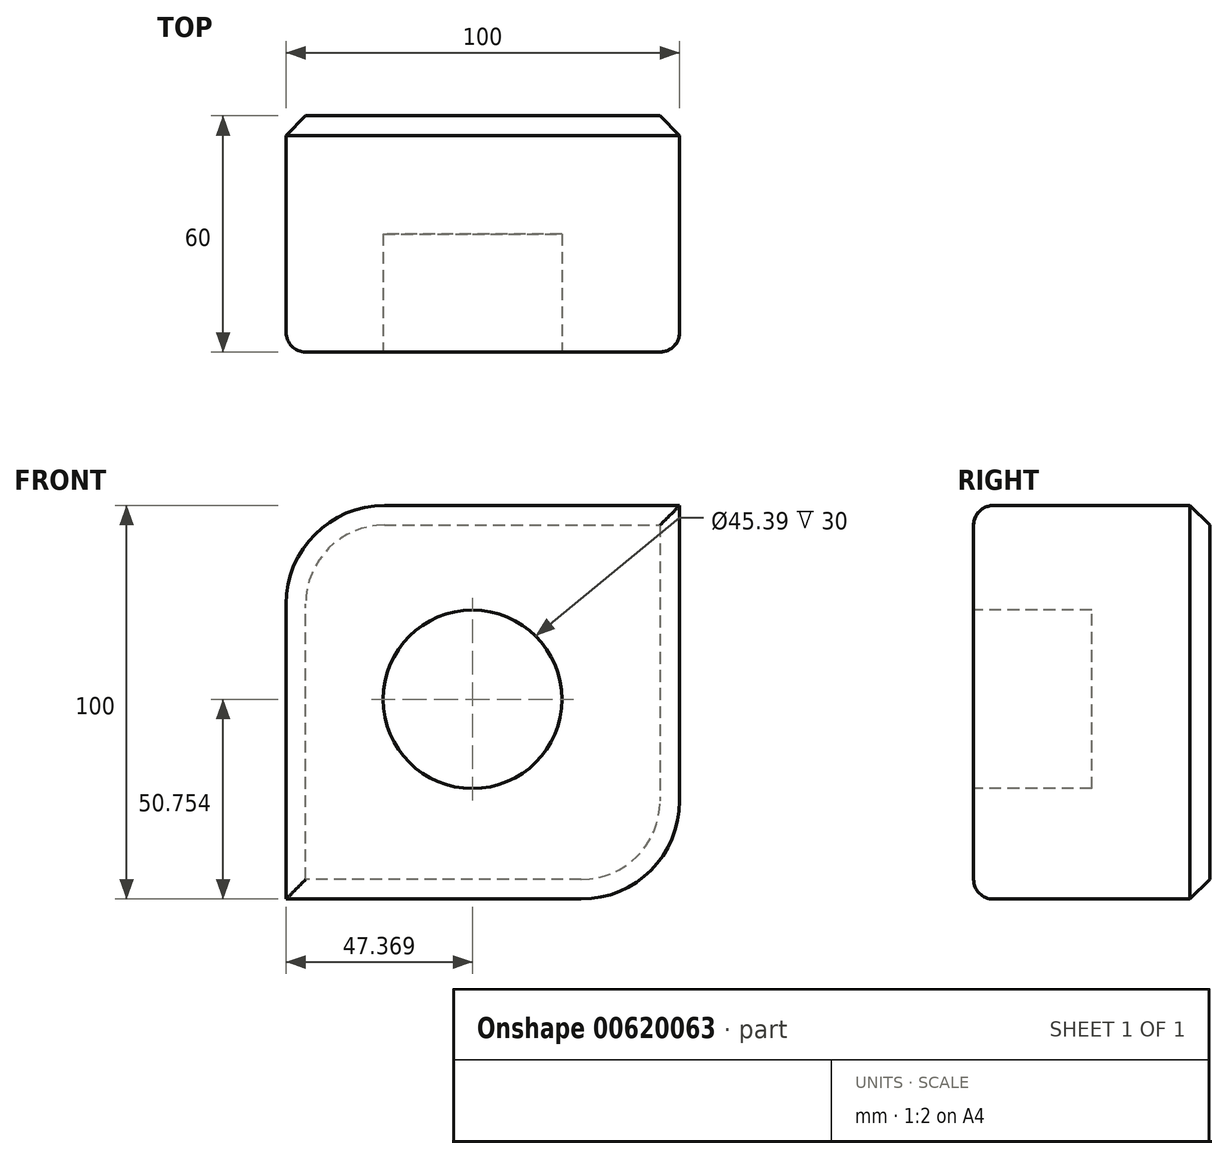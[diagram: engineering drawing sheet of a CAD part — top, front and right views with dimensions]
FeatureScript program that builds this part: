
annotation { "Feature Type Name" : "Feature", "Feature Type Description" : "" }
export const myFeature = defineFeature(function(context is Context, id is Id, definition is map)
    precondition{}
    {
        {
            var Q0;
            Q0=qCreatedBy(makeId("Front.planeOp"),FACE);
            var sketch = newSketch(context, id + "F0", { "sketchPlane" : qUnion([Q0])});
            skLineSegment(sketch, "E0.bottom", {"start": v(-16.3, 72.19) * mm, "end": v(58.7, 72.19) * mm});
            skLineSegment(sketch, "E0.top", {"start": v(-41.3, -27.81) * mm, "end": v(33.7, -27.81) * mm});
            skLineSegment(sketch, "E0.left", {"start": v(-41.3, 47.19) * mm, "end": v(-41.3, -27.81) * mm});
            skLineSegment(sketch, "E0.right", {"start": v(58.7, 72.19) * mm, "end": v(58.7, -2.81) * mm});
            skPoint(sketch, "E1.visualSharp", {"position": v(-41.3, 72.19) * mm});
            skArc(sketch, "E1.filletArc", {"start": v(-16.3, 72.19) * mm, "mid": v(-33.98, 64.87) * mm, "end": v(-41.3, 47.19) * mm});
            skPoint(sketch, "E2.visualSharp", {"position": v(58.7, -27.81) * mm});
            skArc(sketch, "E2.filletArc", {"start": v(33.7, -27.81) * mm, "mid": v(51.38, -20.5) * mm, "end": v(58.7, -2.81) * mm});
            skSolve(sketch);
        }
        {
            var Q0;
            Q0 = qSketchRegion(id + "F0", true);
            extrude(context, id + "F1", {"entities" : qUnion([Q0]), "depth" : 60 * mm, "offsetDistance" : 25 * mm});
        }
        {
            var Q0;
            Q0=makeQuery(id+"F1.opExtrude","CAP_FACE",FACE,{"disambiguationData":[OSD([sQuery(id+"F0.wireOp",EDGE,"E0.bottom"),sQuery(id+"F0.wireOp",EDGE,"E0.top"),sQuery(id+"F0.wireOp",EDGE,"E0.left"),sQuery(id+"F0.wireOp",EDGE,"E0.right"),sQuery(id+"F0.wireOp",EDGE,"E1.filletArc"),sQuery(id+"F0.wireOp",EDGE,"E2.filletArc")])],"isStart":false});
            fillet(context, id + "F2", {"entities" : qUnion([Q0]), "radius" : 5 * mm, "tangentPropagation" : true, "allowEdgeOverflow" : false});
        }
        {
            var Q0;
            Q0=makeQuery(id+"F1.opExtrude","CAP_FACE",FACE,{"disambiguationData":[OSD([sQuery(id+"F0.wireOp",EDGE,"E0.bottom"),sQuery(id+"F0.wireOp",EDGE,"E0.top"),sQuery(id+"F0.wireOp",EDGE,"E0.left"),sQuery(id+"F0.wireOp",EDGE,"E0.right"),sQuery(id+"F0.wireOp",EDGE,"E1.filletArc"),sQuery(id+"F0.wireOp",EDGE,"E2.filletArc")])],"isStart":true});
            chamfer(context, id + "F3", {"entities" : qUnion([Q0]), "width" : 5 * mm, "tangentPropagation" : true});
        }
        {
            var Q0;
            Q0=makeQuery(id+"F1.opExtrude","CAP_FACE",FACE,{"disambiguationData":[OSD([sQuery(id+"F0.wireOp",EDGE,"E0.bottom"),sQuery(id+"F0.wireOp",EDGE,"E0.top"),sQuery(id+"F0.wireOp",EDGE,"E0.left"),sQuery(id+"F0.wireOp",EDGE,"E0.right"),sQuery(id+"F0.wireOp",EDGE,"E1.filletArc"),sQuery(id+"F0.wireOp",EDGE,"E2.filletArc")])],"isStart":false});
            var sketch = newSketch(context, id + "F4", { "sketchPlane" : qUnion([Q0])});
            skCircle(sketch, "E3", {"center": v(6.07, 22.94) * mm, "radius": 22.7 * mm});
            skSolve(sketch);
        }
        {
            var Q0;
            Q0 = qSketchRegion(id + "F4", true);
            extrude(context, id + "F5", {"entities" : qUnion([Q0]), "operationType" : NewBodyOperationType.REMOVE, "oppositeDirection" : true, "depth" : 30 * mm, "offsetDistance" : 25 * mm});
        }
    });
